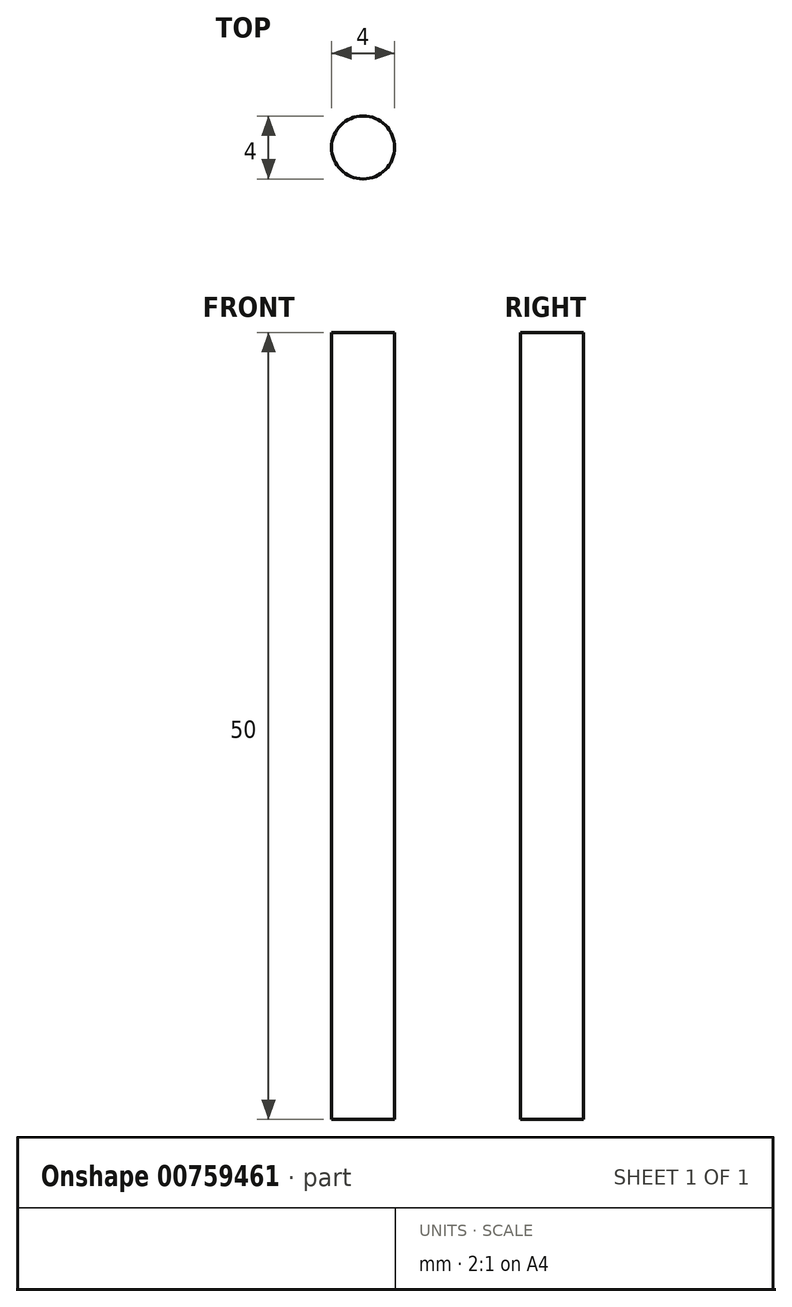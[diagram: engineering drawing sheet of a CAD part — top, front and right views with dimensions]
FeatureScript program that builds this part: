
annotation { "Feature Type Name" : "Feature", "Feature Type Description" : "" }
export const myFeature = defineFeature(function(context is Context, id is Id, definition is map)
    precondition{}
    {
        {
            var Q0;
            Q0=qCreatedBy(makeId("Top.planeOp"),FACE);
            var sketch = newSketch(context, id + "F0", { "sketchPlane" : qUnion([Q0])});
            skCircle(sketch, "E0", {"center": v(0, 0) * mm, "radius": 2 * mm});
            skSolve(sketch);
        }
        {
            var Q0;
            Q0=makeQuery(id+"F0.imprint","IMPRINT",FACE,{"disambiguationData":[TD([[makeQuery(id+"F0.imprint","IMPRINT",EDGE,{"derivedFrom":sQuery(id+"F0.wireOp",EDGE,"E0")}),1.0]])]});
            extrude(context, id + "F1", {"entities" : qUnion([Q0]), "oppositeDirection" : true, "depth" : 50 * mm, "offsetDistance" : 25 * mm});
        }
    });
